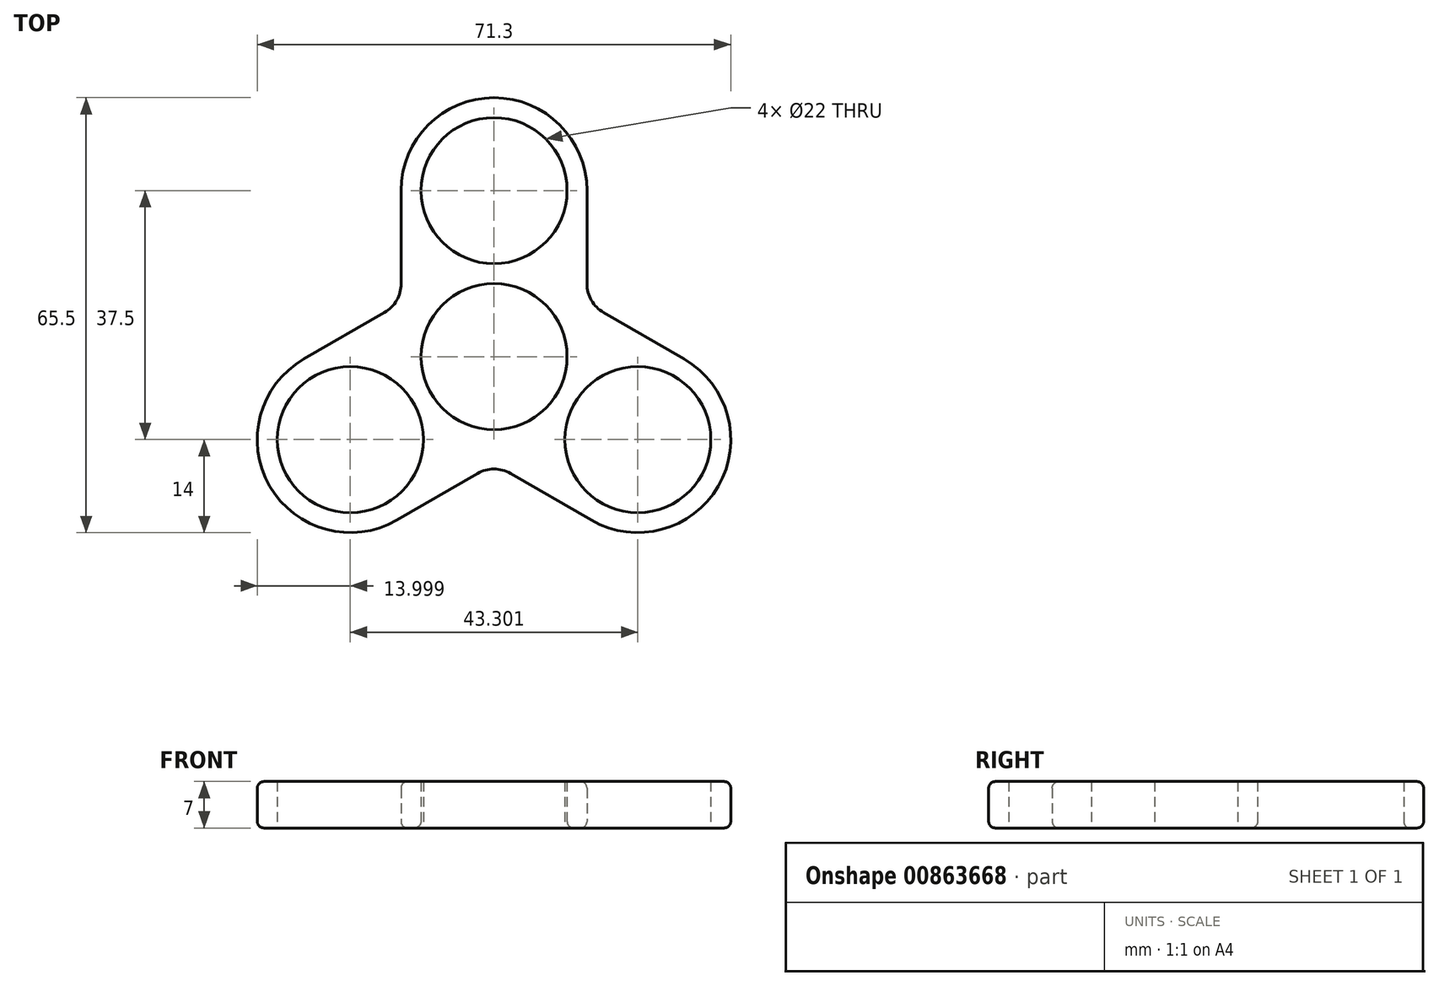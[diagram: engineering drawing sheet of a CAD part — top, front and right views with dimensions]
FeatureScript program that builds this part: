
annotation { "Feature Type Name" : "Feature", "Feature Type Description" : "" }
export const myFeature = defineFeature(function(context is Context, id is Id, definition is map)
    precondition{}
    {
        {
            var Q0;
            Q0=qCreatedBy(makeId("Top.planeOp"),FACE);
            var sketch = newSketch(context, id + "F0", { "sketchPlane" : qUnion([Q0])});
            skCircle(sketch, "E0", {"center": v(0, 0) * mm, "radius": 11 * mm});
            skCircle(sketch, "E1", {"center": v(0, 25) * mm, "radius": 11 * mm});
            skCircle(sketch, "E2.1.0", {"center": v(21.65, -12.5) * mm, "radius": 11 * mm});
            skCircle(sketch, "E2.2.0", {"center": v(-21.65, -12.5) * mm, "radius": 11 * mm});
            skLineSegment(sketch, "E2.anchor1", {"start": v(0, 0) * mm, "end": v(0, 25) * mm, "construction": true});
            skLineSegment(sketch, "E2.anchor2", {"start": v(0, 0) * mm, "end": v(-21.65, -12.5) * mm, "construction": true});
            skArc(sketch, "E3", {"start": v(-14.65, -24.62) * mm, "mid": v(-33.77, -19.5) * mm, "end": v(-28.65, -0.38) * mm});
            skLineSegment(sketch, "E4", {"start": v(-14.65, -24.62) * mm, "end": v(-2.5, -17.6) * mm});
            skLineSegment(sketch, "E5", {"start": v(-28.65, -0.38) * mm, "end": v(-16.5, 6.64) * mm});
            skPoint(sketch, "E6.orphan", {"position": v(0, 16.17) * mm});
            skLineSegment(sketch, "E7.1.0", {"start": v(14.65, -24.62) * mm, "end": v(2.5, -17.6) * mm});
            skArc(sketch, "E7.1.1", {"start": v(28.65, -0.38) * mm, "mid": v(33.77, -19.5) * mm, "end": v(14.65, -24.62) * mm});
            skLineSegment(sketch, "E7.1.2", {"start": v(28.65, -0.38) * mm, "end": v(16.5, 6.64) * mm});
            skLineSegment(sketch, "E7.2.0", {"start": v(14, 25) * mm, "end": v(14, 10.97) * mm});
            skArc(sketch, "E7.2.1", {"start": v(-14, 25) * mm, "mid": v(0, 39) * mm, "end": v(14, 25) * mm});
            skLineSegment(sketch, "E7.2.2", {"start": v(-14, 25) * mm, "end": v(-14, 10.97) * mm});
            skPoint(sketch, "E8.visualSharp", {"position": v(14, 8.08) * mm});
            skArc(sketch, "E8.filletArc", {"start": v(14, 10.97) * mm, "mid": v(14.67, 8.47) * mm, "end": v(16.5, 6.64) * mm});
            skPoint(sketch, "E9.visualSharp", {"position": v(-14, 8.08) * mm});
            skArc(sketch, "E9.filletArc", {"start": v(-16.5, 6.64) * mm, "mid": v(-14.67, 8.47) * mm, "end": v(-14, 10.97) * mm});
            skPoint(sketch, "E10.visualSharp", {"position": v(0, -16.17) * mm});
            skArc(sketch, "E10.filletArc", {"start": v(2.5, -17.6) * mm, "mid": v(0, -16.94) * mm, "end": v(-2.5, -17.6) * mm});
            skSolve(sketch);
        }
        {
            var Q0;
            Q0=qSketchRegion(id+"F0",true);
            extrude(context, id + "F1", {"entities" : qUnion([Q0]), "endBound" : BoundingType.SYMMETRIC, "depth" : 7 * mm, "offsetDistance" : 25 * mm});
        }
        {
            var Q0;
            Q0=makeQuery(id+"F1.opExtrude","CAP_EDGE",EDGE,{"disambiguationData":[OSD([sQuery(id+"F0.wireOp",EDGE,"e28d7eeb-21b6-43dd-9f20-73d8a6c46d7e.2.1")])],"isStart":false});
            var Q1;
            Q1=makeQuery(id+"F1.opExtrude","CAP_EDGE",EDGE,{"disambiguationData":[OSD([sQuery(id+"F0.wireOp",EDGE,"e28d7eeb-21b6-43dd-9f20-73d8a6c46d7e.2.0")])],"isStart":false});
            var Q2;
            Q2=makeQuery(id+"F1.opExtrude","CAP_EDGE",EDGE,{"disambiguationData":[OSD([sQuery(id+"F0.wireOp",EDGE,"9e93f8b0-5c20-4d16-b5f7-98acaeb27eca.filletArc")])],"isStart":false});
            var Q3;
            Q3=makeQuery(id+"F1.opExtrude","CAP_EDGE",EDGE,{"disambiguationData":[OSD([sQuery(id+"F0.wireOp",EDGE,"e28d7eeb-21b6-43dd-9f20-73d8a6c46d7e.1.2")])],"isStart":false});
            var Q4;
            Q4=makeQuery(id+"F1.opExtrude","CAP_EDGE",EDGE,{"disambiguationData":[OSD([sQuery(id+"F0.wireOp",EDGE,"e28d7eeb-21b6-43dd-9f20-73d8a6c46d7e.1.1")])],"isStart":false});
            var Q5;
            Q5=makeQuery(id+"F1.opExtrude","CAP_EDGE",EDGE,{"disambiguationData":[OSD([sQuery(id+"F0.wireOp",EDGE,"e28d7eeb-21b6-43dd-9f20-73d8a6c46d7e.1.0")])],"isStart":false});
            var Q6;
            Q6=makeQuery(id+"F1.opExtrude","CAP_EDGE",EDGE,{"disambiguationData":[OSD([sQuery(id+"F0.wireOp",EDGE,"3d817325-68ea-44a3-8200-b18775fb3d02.filletArc")])],"isStart":false});
            var Q7;
            Q7=makeQuery(id+"F1.opExtrude","CAP_EDGE",EDGE,{"disambiguationData":[OSD([sQuery(id+"F0.wireOp",EDGE,"E4")])],"isStart":false});
            var Q8;
            Q8=makeQuery(id+"F1.opExtrude","CAP_EDGE",EDGE,{"disambiguationData":[OSD([sQuery(id+"F0.wireOp",EDGE,"E3")])],"isStart":false});
            var Q9;
            Q9=makeQuery(id+"F1.opExtrude","CAP_EDGE",EDGE,{"disambiguationData":[OSD([sQuery(id+"F0.wireOp",EDGE,"E5")])],"isStart":false});
            var Q10;
            Q10=makeQuery(id+"F1.opExtrude","CAP_EDGE",EDGE,{"disambiguationData":[OSD([sQuery(id+"F0.wireOp",EDGE,"4dbcd93a-af67-4dae-867c-0d6b9c15ee08.filletArc")])],"isStart":false});
            var Q11;
            Q11=makeQuery(id+"F1.opExtrude","CAP_EDGE",EDGE,{"disambiguationData":[OSD([sQuery(id+"F0.wireOp",EDGE,"e28d7eeb-21b6-43dd-9f20-73d8a6c46d7e.2.2")])],"isStart":false});
            fillet(context, id + "F2", {"entities" : qUnion([Q0, Q1, Q2, Q3, Q4, Q5, Q6, Q7, Q8, Q9, Q10, Q11]), "radius" : 1 * mm, "tangentPropagation" : true, "allowEdgeOverflow" : false});
        }
        {
            var Q0;
            Q0=makeQuery(id+"F1.opExtrude","CAP_EDGE",EDGE,{"disambiguationData":[OSD([sQuery(id+"F0.wireOp",EDGE,"E4")])],"isStart":true});
            var Q1;
            Q1=makeQuery(id+"F1.opExtrude","CAP_EDGE",EDGE,{"disambiguationData":[OSD([sQuery(id+"F0.wireOp",EDGE,"E3")])],"isStart":true});
            var Q2;
            Q2=makeQuery(id+"F1.opExtrude","CAP_EDGE",EDGE,{"disambiguationData":[OSD([sQuery(id+"F0.wireOp",EDGE,"E5")])],"isStart":true});
            var Q3;
            Q3=makeQuery(id+"F1.opExtrude","CAP_EDGE",EDGE,{"disambiguationData":[OSD([sQuery(id+"F0.wireOp",EDGE,"4dbcd93a-af67-4dae-867c-0d6b9c15ee08.filletArc")])],"isStart":true});
            var Q4;
            Q4=makeQuery(id+"F1.opExtrude","CAP_EDGE",EDGE,{"disambiguationData":[OSD([sQuery(id+"F0.wireOp",EDGE,"e28d7eeb-21b6-43dd-9f20-73d8a6c46d7e.2.2")])],"isStart":true});
            var Q5;
            Q5=makeQuery(id+"F1.opExtrude","CAP_EDGE",EDGE,{"disambiguationData":[OSD([sQuery(id+"F0.wireOp",EDGE,"E1")])],"isStart":true});
            var Q6;
            Q6=makeQuery(id+"F1.opExtrude","CAP_EDGE",EDGE,{"disambiguationData":[OSD([sQuery(id+"F0.wireOp",EDGE,"e28d7eeb-21b6-43dd-9f20-73d8a6c46d7e.2.0")])],"isStart":true});
            var Q7;
            Q7=makeQuery(id+"F1.opExtrude","CAP_EDGE",EDGE,{"disambiguationData":[OSD([sQuery(id+"F0.wireOp",EDGE,"9e93f8b0-5c20-4d16-b5f7-98acaeb27eca.filletArc")])],"isStart":true});
            var Q8;
            Q8=makeQuery(id+"F1.opExtrude","CAP_EDGE",EDGE,{"disambiguationData":[OSD([sQuery(id+"F0.wireOp",EDGE,"e28d7eeb-21b6-43dd-9f20-73d8a6c46d7e.1.2")])],"isStart":true});
            var Q9;
            Q9=makeQuery(id+"F1.opExtrude","CAP_EDGE",EDGE,{"disambiguationData":[OSD([sQuery(id+"F0.wireOp",EDGE,"e28d7eeb-21b6-43dd-9f20-73d8a6c46d7e.1.1")])],"isStart":true});
            var Q10;
            Q10=makeQuery(id+"F1.opExtrude","CAP_EDGE",EDGE,{"disambiguationData":[OSD([sQuery(id+"F0.wireOp",EDGE,"e28d7eeb-21b6-43dd-9f20-73d8a6c46d7e.1.0")])],"isStart":true});
            var Q11;
            Q11=makeQuery(id+"F1.opExtrude","CAP_EDGE",EDGE,{"disambiguationData":[OSD([sQuery(id+"F0.wireOp",EDGE,"3d817325-68ea-44a3-8200-b18775fb3d02.filletArc")])],"isStart":true});
            fillet(context, id + "F3", {"entities" : qUnion([Q0, Q1, Q2, Q3, Q4, Q5, Q6, Q7, Q8, Q9, Q10, Q11]), "radius" : 1 * mm, "tangentPropagation" : true, "allowEdgeOverflow" : false});
        }
    });
